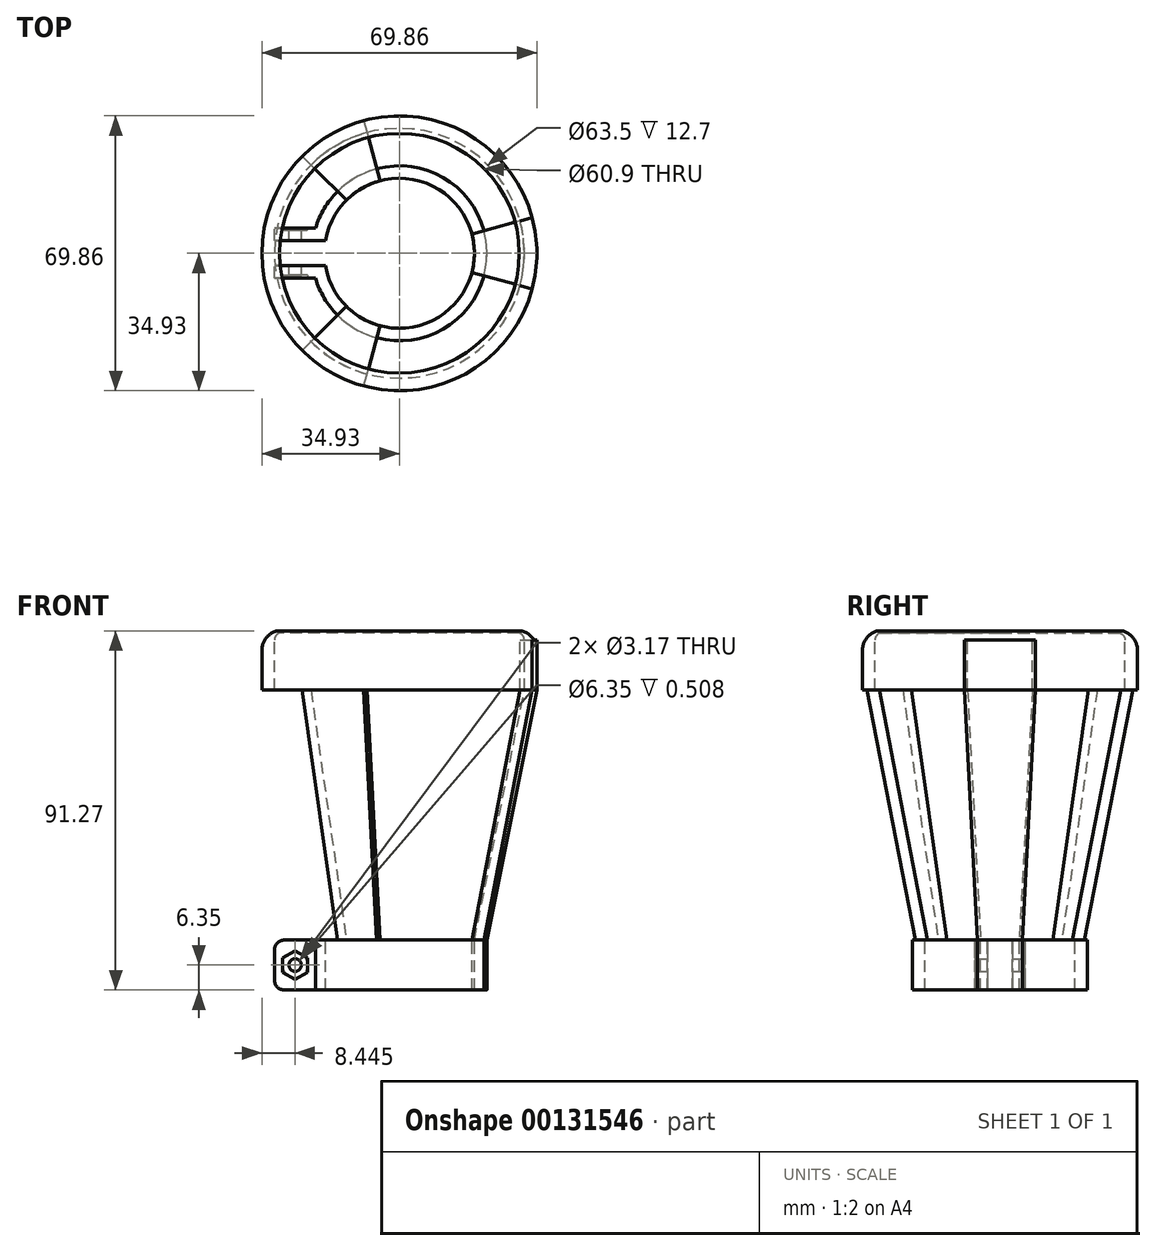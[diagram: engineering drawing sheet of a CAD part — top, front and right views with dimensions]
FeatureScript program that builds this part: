
annotation { "Feature Type Name" : "Feature", "Feature Type Description" : "" }
export const myFeature = defineFeature(function(context is Context, id is Id, definition is map)
    precondition{}
    {
        {
            var Q0;
            Q0=qCreatedBy(makeId("Front.planeOp"),FACE);
            var sketch = newSketch(context, id + "F0", { "sketchPlane" : qUnion([Q0])});
            skLineSegment(sketch, "E0.bottom", {"start": v(19.05, -6.35) * mm, "end": v(-19.05, -6.35) * mm});
            skLineSegment(sketch, "E0.top", {"start": v(19.05, 6.35) * mm, "end": v(-19.05, 6.35) * mm});
            skLineSegment(sketch, "E0.left", {"start": v(19.05, -6.35) * mm, "end": v(19.05, 6.35) * mm});
            skLineSegment(sketch, "E0.right", {"start": v(-19.05, -6.35) * mm, "end": v(-19.05, 6.35) * mm});
            skPoint(sketch, "E0.middle", {"position": v(0, 0) * mm});
            skLineSegment(sketch, "E1.top", {"start": v(31.75, 82.55) * mm, "end": v(-31.75, 82.55) * mm});
            skLineSegment(sketch, "E1.left", {"start": v(31.75, 69.85) * mm, "end": v(31.75, 82.55) * mm});
            skLineSegment(sketch, "E1.right", {"start": v(-31.75, 69.85) * mm, "end": v(-31.75, 82.55) * mm});
            skPoint(sketch, "E1.middle", {"position": v(0, 76.2) * mm});
            skPoint(sketch, "E2.middle", {"position": v(0, 38.1) * mm});
            skLineSegment(sketch, "E3", {"start": v(31.75, 82.55) * mm, "end": v(34.92, 82.55) * mm});
            skLineSegment(sketch, "E4", {"start": v(34.92, 82.55) * mm, "end": v(34.92, 69.85) * mm});
            skLineSegment(sketch, "E5", {"start": v(34.92, 69.85) * mm, "end": v(31.75, 69.85) * mm});
            skLineSegment(sketch, "E6", {"start": v(19.05, 6.35) * mm, "end": v(22.22, 6.35) * mm});
            skLineSegment(sketch, "E7", {"start": v(22.22, 6.35) * mm, "end": v(22.23, -6.35) * mm});
            skLineSegment(sketch, "E8", {"start": v(22.23, -6.35) * mm, "end": v(19.05, -6.35) * mm});
            skLineSegment(sketch, "E9", {"start": v(0, 82.55) * mm, "end": v(0, -6.35) * mm, "construction": true});
            skLineSegment(sketch, "E10.bottom", {"start": v(-26.08, -10.35) * mm, "end": v(-12.02, -10.35) * mm});
            skLineSegment(sketch, "E10.top", {"start": v(-26.08, 10.35) * mm, "end": v(-12.02, 10.35) * mm});
            skLineSegment(sketch, "E10.left", {"start": v(-26.08, -10.35) * mm, "end": v(-26.08, 10.35) * mm});
            skLineSegment(sketch, "E10.right", {"start": v(-12.02, -10.35) * mm, "end": v(-12.02, 10.35) * mm});
            skPoint(sketch, "E10.middle", {"position": v(-19.05, 0) * mm});
            skLineSegment(sketch, "E11", {"start": v(-19.05, 6.35) * mm, "end": v(-29.21, 6.35) * mm});
            skLineSegment(sketch, "E12", {"start": v(-31.75, 3.8) * mm, "end": v(-31.75, -3.8) * mm});
            skLineSegment(sketch, "E13", {"start": v(-29.21, -6.35) * mm, "end": v(-19.05, -6.35) * mm});
            skPoint(sketch, "E14.visualSharp", {"position": v(-31.75, 6.35) * mm});
            skArc(sketch, "E14.filletArc", {"start": v(-29.21, 6.35) * mm, "mid": v(-31, 5.6) * mm, "end": v(-31.75, 3.8) * mm});
            skPoint(sketch, "E15.visualSharp", {"position": v(-31.75, -6.35) * mm});
            skArc(sketch, "E15.filletArc", {"start": v(-31.75, -3.8) * mm, "mid": v(-31, -5.6) * mm, "end": v(-29.21, -6.35) * mm});
            skArc(sketch, "E16", {"start": v(31.75, 82.55) * mm, "mid": v(31.4, 83.68) * mm, "end": v(30.45, 84.39) * mm});
            skLineSegment(sketch, "E17", {"start": v(30.45, 84.39) * mm, "end": v(34.92, 84.39) * mm});
            skLineSegment(sketch, "E18", {"start": v(34.92, 84.39) * mm, "end": v(34.92, 82.55) * mm});
            skLineSegment(sketch, "E19", {"start": v(30.45, 84.39) * mm, "end": v(30.45, 85.02) * mm});
            skLineSegment(sketch, "E20", {"start": v(30.45, 85.02) * mm, "end": v(34.92, 85.02) * mm});
            skLineSegment(sketch, "E21", {"start": v(34.92, 85.02) * mm, "end": v(34.92, 84.39) * mm});
            skLineSegment(sketch, "E22", {"start": v(-31.75, 69.85) * mm, "end": v(31.75, 69.85) * mm});
            skSolve(sketch);
        }
        {
            var Q0;
            Q0=makeQuery(id+"F0.imprint","IMPRINT",FACE,{"disambiguationData":[TD([[makeQuery(id+"F0.imprint","IMPRINT",EDGE,{"derivedFrom":sQuery(id+"F0.wireOp",EDGE,"E1.left")}),-1.0]])]});
            var Q1;
            Q1=makeQuery(id+"F0.imprint","IMPRINT",FACE,{"disambiguationData":[TD([[makeQuery(id+"F0.imprint","IMPRINT",EDGE,{"derivedFrom":sQuery(id+"F0.wireOp",EDGE,"E0.left")}),-1.0]])]});
            var Q2;
            Q2=sQuery(id+"F0.wireOp",EDGE,"E9");
            revolve(context, id + "F1", {"entities" : qUnion([Q0, Q1]), "axis" : qUnion([Q2]), "revolveType" : RevolveType.TWO_DIRECTIONS, "angle" : 15 * degree, "angleBack" : 345 * degree});
        }
        {
            var Q0;
            Q0=makeQuery(id+"F1.opRevolve","SWEPT_FACE",FACE,{"disambiguationData":[OSD([sQuery(id+"F0.wireOp",EDGE,"E5")])]});
            var Q1;
            Q1=makeQuery(id+"F1.opRevolve","SWEPT_FACE",FACE,{"disambiguationData":[OSD([sQuery(id+"F0.wireOp",EDGE,"E6")])]});
            loft(context, id + "F2", {"sheetProfilesArray" : [{ "sheetProfileEntities" : qUnion([Q0]) }, { "sheetProfileEntities" : qUnion([Q1]) }]});
        }
        {
            var Q0;
            Q0=makeQuery(id+"F0.imprint","IMPRINT",FACE,{"disambiguationData":[TD([[makeQuery(id+"F0.imprint","IMPRINT",EDGE,{"derivedFrom":sQuery(id+"F0.wireOp",EDGE,"E1.left")}),-1.0]])]});
            var Q1;
            Q1=makeQuery(id+"F0.imprint","IMPRINT",FACE,{"disambiguationData":[TD([[makeQuery(id+"F0.imprint","IMPRINT",EDGE,{"derivedFrom":sQuery(id+"F0.wireOp",EDGE,"E0.left")}),-1.0]])]});
            var Q2;
            Q2=makeQuery(id+"F0.imprint","IMPRINT",FACE,{"disambiguationData":[TD([[makeQuery(id+"F0.imprint","IMPRINT",EDGE,{"derivedFrom":sQuery(id+"F0.wireOp",EDGE,"E3")}),1.0]])]});
            var Q3;
            Q3=makeQuery(id+"F0.imprint","IMPRINT",FACE,{"disambiguationData":[TD([[makeQuery(id+"F0.imprint","IMPRINT",EDGE,{"derivedFrom":sQuery(id+"F0.wireOp",EDGE,"E17")}),1.0]])]});
            var Q4;
            Q4=sQuery(id+"F0.wireOp",EDGE,"E9");
            revolve(context, id + "F3", {"entities" : qUnion([Q0, Q1, Q2, Q3]), "axis" : qUnion([Q4]), "revolveType" : RevolveType.FULL});
        }
        {
            var Q0;
            Q0=makeQuery(id+"F2.opLoft","SWEPT_BODY",BODY,{"disambiguationData":[OSD([sQuery(id+"F0.wireOp",EDGE,"E5"),sQuery(id+"F0.wireOp",EDGE,"E6")])]});
            var Q1;
            Q1=sQuery(id+"F0.wireOp",EDGE,"E9");
            circularPattern(context, id + "F4", {"entities" : qUnion([Q0]), "axis" : qUnion([Q1]), "angle" : 120 * degree, "instanceCount" : 3});
        }
        {
            var Q0;
            Q0=makeQuery(id+"F0.imprint","IMPRINT",FACE,{"disambiguationData":[TD([[makeQuery(id+"F0.imprint","IMPRINT",EDGE,{"derivedFrom":sQuery(id+"F0.wireOp",EDGE,"E12")}),1.0]])]});
            var Q1;
            {var subQ0=sQuery(id+"F0.wireOp",EDGE,"E0.right");Q1=makeQuery(id+"F0.imprint","IMPRINT",FACE,{"disambiguationData":[TD([[makeQuery(id+"F0.imprint","IMPRINT",EDGE,{"derivedFrom":subQ0}),1.0]])]});}
            extrude(context, id + "F5", {"entities" : qUnion([Q0, Q1]), "operationType" : NewBodyOperationType.ADD, "endBound" : BoundingType.SYMMETRIC, "depth" : 12.7 * mm});
        }
        {
            var Q0;
            {var subQ1=sQuery(id+"F0.wireOp",EDGE,"E10.top");Q0=makeQuery(id+"F0.imprint","IMPRINT",FACE,{"disambiguationData":[TD([[makeQuery(id+"F0.imprint","IMPRINT",EDGE,{"derivedFrom":subQ1}),-1.0]])]});}
            var Q1;
            {var subQ1=sQuery(id+"F0.wireOp",EDGE,"E10.bottom");Q1=makeQuery(id+"F0.imprint","IMPRINT",FACE,{"disambiguationData":[TD([[makeQuery(id+"F0.imprint","IMPRINT",EDGE,{"derivedFrom":subQ1}),1.0]])]});}
            var Q2;
            {var subQ0=sQuery(id+"F0.wireOp",EDGE,"E0.right");Q2=makeQuery(id+"F0.imprint","IMPRINT",FACE,{"disambiguationData":[TD([[makeQuery(id+"F0.imprint","IMPRINT",EDGE,{"derivedFrom":subQ0}),-1.0]])]});}
            var Q3;
            {var subQ0=sQuery(id+"F0.wireOp",EDGE,"E0.right");Q3=makeQuery(id+"F0.imprint","IMPRINT",FACE,{"disambiguationData":[TD([[makeQuery(id+"F0.imprint","IMPRINT",EDGE,{"derivedFrom":subQ0}),1.0]])]});}
            var Q4;
            Q4=makeQuery(id+"F0.imprint","IMPRINT",FACE,{"disambiguationData":[TD([[makeQuery(id+"F0.imprint","IMPRINT",EDGE,{"derivedFrom":sQuery(id+"F0.wireOp",EDGE,"E12")}),1.0]])]});
            extrude(context, id + "F6", {"entities" : qUnion([Q0, Q1, Q2, Q3, Q4]), "operationType" : NewBodyOperationType.REMOVE, "endBound" : BoundingType.SYMMETRIC, "depth" : 6.35 * mm});
        }
        {
            var Q0;
            Q0=makeQuery(id+"F5.opExtrude","CAP_FACE",FACE,{"disambiguationData":[OSD([sQuery(id+"F0.wireOp",EDGE,"E0.right"),sQuery(id+"F0.wireOp",EDGE,"E11"),sQuery(id+"F0.wireOp",EDGE,"E12"),sQuery(id+"F0.wireOp",EDGE,"E13"),sQuery(id+"F0.wireOp",EDGE,"E14.filletArc"),sQuery(id+"F0.wireOp",EDGE,"E15.filletArc")])],"isStart":true});
            var sketch = newSketch(context, id + "F7", { "sketchPlane" : qUnion([Q0])});
            skLineSegment(sketch, "E23", {"start": v(21.3, 0) * mm, "end": v(31.75, 0) * mm});
            skLineSegment(sketch, "E24", {"start": v(26.49, 6.35) * mm, "end": v(26.49, 0) * mm});
            skLineSegment(sketch, "E25", {"start": v(26.49, 0) * mm, "end": v(26.49, -6.35) * mm});
            skSolve(sketch);
        }
        {
            var Q0;
            Q0=sQuery(id+"F7.wireOp",VERTEX,"E25.start");
            var Q1;
            Q1=makeQuery(id+"F3.opRevolve","SWEPT_BODY",BODY,{"disambiguationData":[OSD([sQuery(id+"F0.wireOp",EDGE,"E0.left"),sQuery(id+"F0.wireOp",EDGE,"E6"),sQuery(id+"F0.wireOp",EDGE,"E7"),sQuery(id+"F0.wireOp",EDGE,"E8")])]});
            hole(context, id + "F8", {"style" : HoleStyle.C_BORE, "endStyle" : HoleEndStyle.THROUGH, "holeDiameter" : 3.17 * mm, "cBoreDiameter" : 6.35 * mm, "cBoreDepth" : 0.5 * mm, "locations" : qUnion([Q0]), "scope" : qUnion([Q1]), "isTappedThrough" : true});
        }
        {
            var Q0;
            Q0=makeQuery(id+"F5.opExtrude","CAP_FACE",FACE,{"disambiguationData":[OSD([sQuery(id+"F0.wireOp",EDGE,"E0.right"),sQuery(id+"F0.wireOp",EDGE,"E11"),sQuery(id+"F0.wireOp",EDGE,"E12"),sQuery(id+"F0.wireOp",EDGE,"E13"),sQuery(id+"F0.wireOp",EDGE,"E14.filletArc"),sQuery(id+"F0.wireOp",EDGE,"E15.filletArc")])],"isStart":false});
            var sketch = newSketch(context, id + "F9", { "sketchPlane" : qUnion([Q0])});
            skCircle(sketch, "E26.cCircle", {"center": v(-26.49, 0) * mm, "radius": 3.18 * mm, "construction": true});
            skLineSegment(sketch, "E26.0", {"start": v(-23.31, -1.83) * mm, "end": v(-26.49, -3.67) * mm});
            skLineSegment(sketch, "E26.1", {"start": v(-26.49, -3.67) * mm, "end": v(-29.66, -1.83) * mm});
            skLineSegment(sketch, "E26.2", {"start": v(-29.66, -1.83) * mm, "end": v(-29.66, 1.83) * mm});
            skLineSegment(sketch, "E26.3", {"start": v(-29.66, 1.83) * mm, "end": v(-26.49, 3.67) * mm});
            skLineSegment(sketch, "E26.4", {"start": v(-26.49, 3.67) * mm, "end": v(-23.31, 1.83) * mm});
            skLineSegment(sketch, "E26.5", {"start": v(-23.31, 1.83) * mm, "end": v(-23.31, -1.83) * mm});
            skPoint(sketch, "E26.0.midPoint", {"position": v(-24.9, -2.75) * mm});
            skSolve(sketch);
        }
        {
            var Q0;
            Q0=makeQuery(id+"F9.imprint","IMPRINT",FACE,{"disambiguationData":[TD([[makeQuery(id+"F9.imprint","IMPRINT",EDGE,{"derivedFrom":sQuery(id+"F9.wireOp",EDGE,"E26.0")}),-1.0]])]});
            extrude(context, id + "F10", {"entities" : qUnion([Q0]), "operationType" : NewBodyOperationType.REMOVE, "oppositeDirection" : true, "depth" : 0.76 * mm});
        }
        {
            var Q0;
            Q0=makeQuery(id+"F3.opRevolve","SWEPT_EDGE",EDGE,{"disambiguationData":[OSD([sQuery(id+"F0.wireOp",EDGE,"E20"),sQuery(id+"F0.wireOp",EDGE,"E21")])]});
            fillet(context, id + "F11", {"entities" : qUnion([Q0]), "radius" : 5.08 * mm, "tangentPropagation" : true, "allowEdgeOverflow" : false});
        }
        {
            var Q0;
            Q0=makeQuery(id+"F11.opFillet","BLEND_EDGE",EDGE,{"blendedFrom":[makeQuery(id+"F3.opRevolve","SWEPT_EDGE",EDGE,{"disambiguationData":[OSD([sQuery(id+"F0.wireOp",EDGE,"E20"),sQuery(id+"F0.wireOp",EDGE,"E21")])]}),makeQuery(id+"F3.opRevolve","SWEPT_FACE",FACE,{"disambiguationData":[OSD([sQuery(id+"F0.wireOp",EDGE,"E19")])]})],"blendedInto":[makeQuery(id+"F3.opRevolve","SWEPT_FACE",FACE,{"disambiguationData":[OSD([sQuery(id+"F0.wireOp",EDGE,"E19")])]})]});
            fillet(context, id + "F12", {"entities" : qUnion([Q0]), "radius" : 0.5 * mm, "tangentPropagation" : true, "allowEdgeOverflow" : false});
        }
    });
